# Revit family: HUNTER_Flow-Clik Sensor
name_source: partatom
category: Pipe Fittings
revit_build: Autodesk Revit 2017 (Build: 20160225_1515(x64)
units: mm (PartAtom-declared; Revit-internal decimal feet)

## family parameters
Always vertical = Yes
Cut with Voids When Loaded = No
OmniClass Number = 23.27.11.15.23
OmniClass Title = Flow Sensors
Part Type = Tee
Round Connector Dimension = Use Diameter
Shared = Yes
Work Plane-Based = No

## types (8) — shared parameters
Assembly Code = G4030100
Input Voltage = 24 V
Keynote = 328423.05
Loss Method = K Coefficient
Manufacturer = Hunter® Industries
URL = https://www.hunterindustries.com

## per-type parameters (varying)
| type | Adapter for FCT | Cap_Dia | Connector Diameter | Description | FCT Symbol | Flow | Half_Dia | Length | Minimum Flow | Operating Flow | Pipe Connector BSP | Pipe ID | Pipe OD | Pipe_Dia | Sensor_Length | Suggested Maximum Flow | Type Comments |
| FCT-100 | BSP 1" (25mm) adapter | 19 mm | 25 mm  [stored 0.082021 ft] | FLOW-CLIK® -1" (25mm) Schedule 40 Sensor receptacle tee | FCT-100 : SYMBOL | 64.00 L/min | 17 mm | 50 mm  [stored 0.164042 ft] | 7.60 L/min | 64.00 L/min | 25 mm  [stored 0.082021 ft] | 27 mm | 33 mm | 33 mm | 100 mm  [stored 0.328084 ft] | 64.00 L/min | FLOW-CLIK® - FCT-100 Flow Sensor |
| FCT-150 | BSP 1 1/2" (40mm) adapter | 26 mm | 40 mm  [stored 0.131234 ft] | FLOW-CLIK® -1 1/2" (40mm) Schedule 40 Sensor receptacle tee | FCT-150 : SYMBOL | 132.00 L/min | 24 mm | 73 mm | 19.00 L/min | 132.00 L/min | 40 mm  [stored 0.131234 ft] | 41 mm | 48 mm | 48 mm | 145 mm | 132.00 L/min | FLOW-CLIK® - FCT-150 Flow Sensor |
| FCT-158 | BSP 1 1/2" (40mm) adapter | 26 mm | 40 mm  [stored 0.131234 ft] | FLOW-CLIK® -1 1/2" (40mm) Schedule 80 Sensor receptacle tee | FCT-158 : SYMBOL | 132.00 L/min | 24 mm | 73 mm | 19.00 L/min | 132.00 L/min | 40 mm  [stored 0.131234 ft] | 38 mm | 48 mm | 48 mm | 145 mm | 132.00 L/min | FLOW-CLIK® - FCT-158 Flow Sensor |
| FCT-200 | BSP 2" (50mm) adapter | 32 mm | 50 mm  [stored 0.164042 ft] | FLOW-CLIK® -2" (50mm) Schedule 40 Sensor receptacle tee | FCT-200 : SYMBOL | 208.00 L/min | 30 mm | 91 mm | 37.80 L/min | 208.00 L/min | 50 mm  [stored 0.164042 ft] | 53 mm | 60 mm | 60 mm | 181 mm | 208.00 L/min | FLOW-CLIK® - FCT-200 Flow Sensor |
| FCT-208 | BSP 2" (50mm) adapter | 32 mm | 50 mm  [stored 0.164042 ft] | FLOW-CLIK® -2" (50mm) Schedule 80 Sensor receptacle tee | FCT-208 : SYMBOL | 208.00 L/min | 30 mm | 91 mm | 37.80 L/min | 208.00 L/min | 50 mm  [stored 0.164042 ft] | 49 mm | 60 mm | 60 mm | 181 mm | 208.00 L/min | FLOW-CLIK® - FCT-208 Flow Sensor |
| FCT-300 | BSP 3" (80mm) adapter | 47 mm | 80 mm  [stored 0.262467 ft] | FLOW-CLIK® -3" (80mm) Schedule 40 Sensor receptacle tee | FCT-300 : SYMBOL | 450.00 L/min | 45 mm | 134 mm | 106.00 L/min | 450.00 L/min | 80 mm  [stored 0.262467 ft] | 78 mm | 89 mm  [stored 0.291995 ft] | 89 mm  [stored 0.291995 ft] | 267 mm  [stored 0.875984 ft] | 450.00 L/min | FLOW-CLIK® - FCT-300 Flow Sensor |
| FCT-308 | BSP 3" (80mm) adapter | 47 mm | 80 mm  [stored 0.262467 ft] | FLOW-CLIK® -3" (80mm) Schedule 80 Sensor receptacle tee | FCT-308 : SYMBOL | 450.00 L/min | 45 mm | 134 mm | 106.00 L/min | 450.00 L/min | 80 mm  [stored 0.262467 ft] | 74 mm | 89 mm  [stored 0.291995 ft] | 89 mm  [stored 0.291995 ft] | 267 mm  [stored 0.875984 ft] | 450.00 L/min | FLOW-CLIK® - FCT-308 Flow Sensor |
| FCT-400 | BSP 4" (100mm) adapter | 59 mm | 100 mm  [stored 0.328084 ft] | FLOW-CLIK® -4" (100mm) Schedule 40 Sensor receptacle tee | FCT-400 : SYMBOL | 750.00 L/min | 57 mm | 172 mm | 129.00 L/min | 750.00 L/min | 100 mm  [stored 0.328084 ft] | 102 mm | 114 mm | 114 mm | 343 mm | 750.00 L/min | FLOW-CLIK® - FCT-400 Flow Sensor |

note: column(s) folded — value = type name in every type: Model

note: [stored X ft] marks values corroborated as IEEE doubles in the binary element streams (Revit-internal decimal feet)

## geometry (parser evidence)
native form markers: Sweep x9
no freeform markers — native parametric forms only
